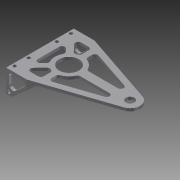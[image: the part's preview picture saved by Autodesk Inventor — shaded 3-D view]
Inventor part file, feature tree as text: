
AUTODESK INVENTOR PART (.ipt)
format: ipt  version: 2012 (Build 160160000, 160)  size: 291,328 bytes
history: native  units: in
note: dims shown in document units (in); Inventor stores cm internally (conversion verified against a paired STEP export)
features: extrude x4, sketch x3, fillet x3, hole x1
ambient origin geometry x8: Origin, YZ Plane, XZ Plane, XY Plane, X Axis, Y Axis, Z Axis, Center Point
bodies: Solid1 (feature_tree)
feature tree (11):
  sketch  "Sketch1"  dims[d0=2.75in d1=4.0in]
  extrude  "Extrusion1"  Depth=4.0in
  extrude  "Extrusion2"  Depth=0.1279in
  fillet  "Fillet1"  Radius=0.375in
  hole  "Hole1"  [1 undecoded]
  sketch  "Sketch2"  dims[d2=1.375in d6=0.1279in d7=0.375in]
  fillet  "Fillet6"  Radius=0.125in
  extrude  "Extrusion7"  Depth=0.625in
  extrude  "Extrusion8"  Depth=0.1875in
  fillet  "Fillet8"  Radius=0.1875in
  sketch  "Sketch4"  dims[d8=1.289in d9=0.875in d10=0.125in d11=0.0in d12=0.625in d13=0.1875in d14=0.1875in d15=0.25in d16=0.25in d17=0.125in d18=0.125in d19=0.125in d20=0.125in d21=0.125in d22=0.125in d24=0.125in d25=0.125in d26=0.25in d27=0.375in d28=0.25in d29=0.125in d30=0.0in d31=0.125in d32=0.125in d33=0.125in d35=0.125in d36=0.125in d38=0.144in d39=0.75in d40=0.25in d41=0.25in d42=0.5635in d43=1.0in d44=0.8108in d51=0.125in d53=0.875in d54=0.0625in d62=0.75in d63=0.75in d69=0.125in d70=0.1279in d71=0.4375in d73=0.125in d75=0.125in d76=0.125in d77=1.0in d78=0.0in d79=0.125in d80=0.125in d81=0.136in d82=0.125in d83=0.25in d84=0.125in d85=0.1875in d86=0.125in d87=0.125in d88=1.0in d89=0.0in d90=0.125in]
note: 1 required parameter value undecoded (feature->parameter linkage not recoverable at this tier; creation-order binding heuristic only, values carry confidence <= 0.55)
